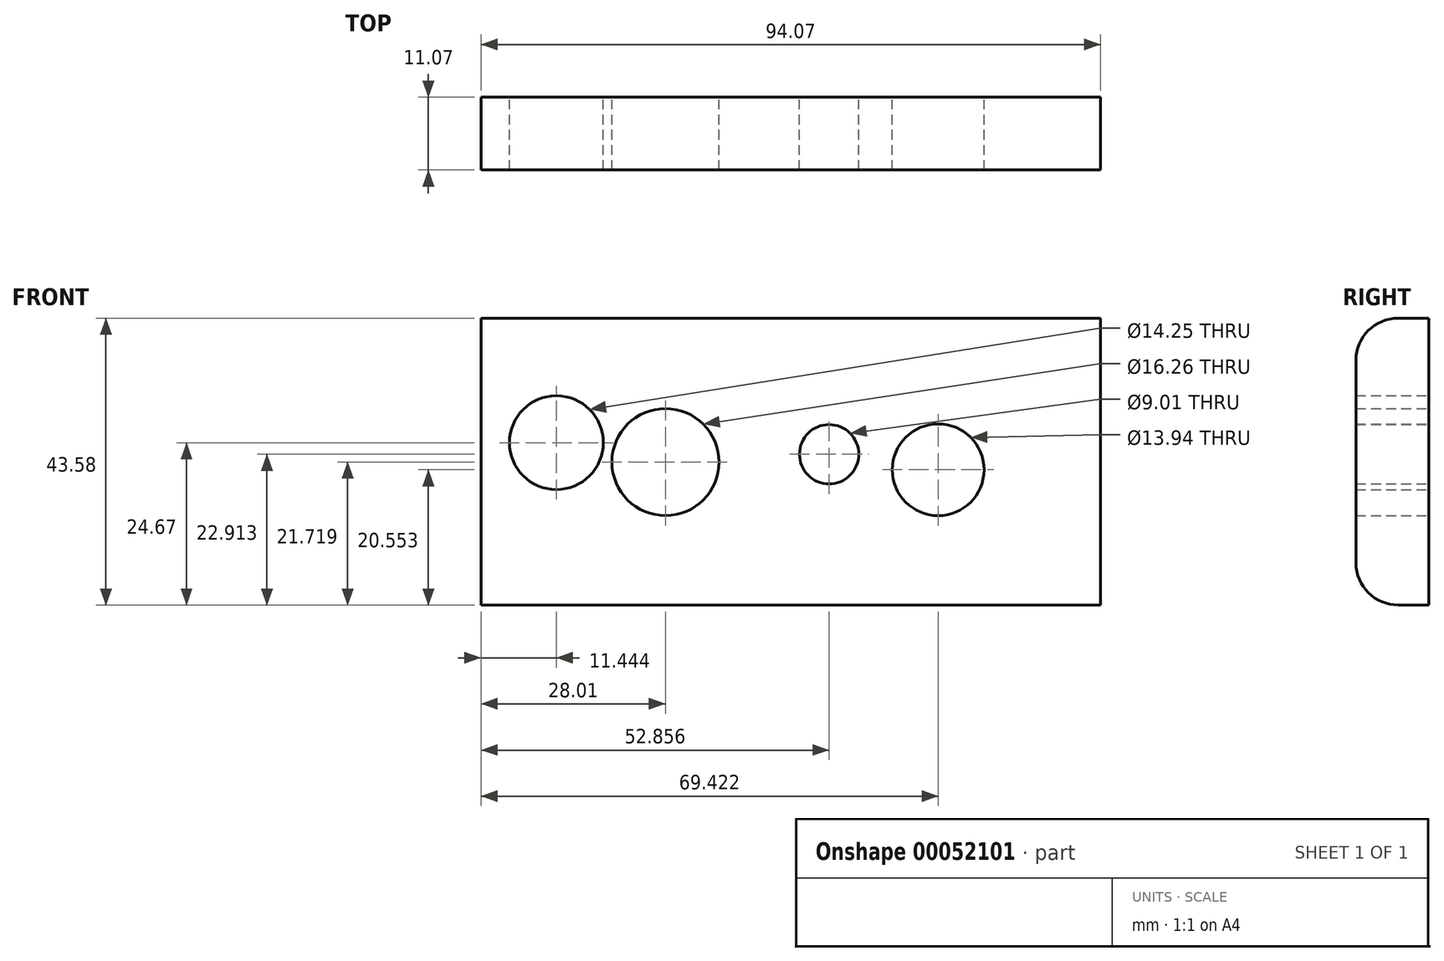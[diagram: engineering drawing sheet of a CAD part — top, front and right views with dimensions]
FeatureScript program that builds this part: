
annotation { "Feature Type Name" : "Feature", "Feature Type Description" : "" }
export const myFeature = defineFeature(function(context is Context, id is Id, definition is map)
    precondition{}
    {
        {
            var Q0;
            Q0=qCreatedBy(makeId("Front.planeOp"),FACE);
            var sketch = newSketch(context, id + "F0", { "sketchPlane" : qUnion([Q0])});
            skLineSegment(sketch, "E0.bottom", {"start": v(-38.08, 13.17) * mm, "end": v(55.99, 13.17) * mm});
            skLineSegment(sketch, "E0.top", {"start": v(-38.08, -30.4) * mm, "end": v(55.99, -30.4) * mm});
            skLineSegment(sketch, "E0.left", {"start": v(-38.08, 13.17) * mm, "end": v(-38.08, -30.4) * mm});
            skLineSegment(sketch, "E0.right", {"start": v(55.99, 13.17) * mm, "end": v(55.99, -30.4) * mm});
            skSolve(sketch);
        }
        {
            var Q0;
            Q0=makeQuery(id+"F0.imprint","IMPRINT",FACE,{"disambiguationData":[TD([[makeQuery(id+"F0.imprint","IMPRINT",EDGE,{"derivedFrom":sQuery(id+"F0.wireOp",EDGE,"E0.bottom")}),-1.0]])]});
            extrude(context, id + "F1", {"entities" : qUnion([Q0]), "depth" : 11.07 * mm});
        }
        {
            var Q0;
            Q0=qCreatedBy(makeId("Front.planeOp"),FACE);
            var sketch = newSketch(context, id + "F2", { "sketchPlane" : qUnion([Q0])});
            skCircle(sketch, "E1", {"center": v(-26.64, -5.74) * mm, "radius": 7.12 * mm});
            skCircle(sketch, "E2", {"center": v(-10.07, -8.7) * mm, "radius": 8.13 * mm});
            skCircle(sketch, "E3", {"center": v(14.78, -7.5) * mm, "radius": 4.5 * mm});
            skCircle(sketch, "E4", {"center": v(31.34, -9.86) * mm, "radius": 6.97 * mm});
            skSolve(sketch);
        }
        {
            var Q0;
            Q0=makeQuery(id+"F2.imprint","IMPRINT",FACE,{"disambiguationData":[TD([[makeQuery(id+"F2.imprint","IMPRINT",EDGE,{"derivedFrom":sQuery(id+"F2.wireOp",EDGE,"E4")}),1.0]])]});
            var Q1;
            Q1=makeQuery(id+"F2.imprint","IMPRINT",FACE,{"disambiguationData":[TD([[makeQuery(id+"F2.imprint","IMPRINT",EDGE,{"derivedFrom":sQuery(id+"F2.wireOp",EDGE,"E3")}),1.0]])]});
            var Q2;
            Q2=makeQuery(id+"F2.imprint","IMPRINT",FACE,{"disambiguationData":[TD([[makeQuery(id+"F2.imprint","IMPRINT",EDGE,{"derivedFrom":sQuery(id+"F2.wireOp",EDGE,"E2")}),1.0]])]});
            var Q3;
            Q3=makeQuery(id+"F2.imprint","IMPRINT",FACE,{"disambiguationData":[TD([[makeQuery(id+"F2.imprint","IMPRINT",EDGE,{"derivedFrom":sQuery(id+"F2.wireOp",EDGE,"E1")}),1.0]])]});
            var Q4;
            Q4=sQuery(id+"F2.wireOp",EDGE,"E1");
            var Q5;
            Q5=sQuery(id+"F2.wireOp",EDGE,"E2");
            var Q6;
            Q6=sQuery(id+"F2.wireOp",EDGE,"E3");
            var Q7;
            Q7=sQuery(id+"F2.wireOp",EDGE,"E4");
            extrude(context, id + "F3", {"entities" : qUnion([Q0, Q1, Q2, Q3]), "operationType" : NewBodyOperationType.REMOVE, "surfaceEntities" : qUnion([Q4, Q5, Q6, Q7]), "endBound" : BoundingType.UP_TO_NEXT, "depth" : 25.4 * mm});
        }
        {
            var Q0;
            Q0=makeQuery(id+"F1.opExtrude","CAP_EDGE",EDGE,{"disambiguationData":[OSD([sQuery(id+"F0.wireOp",EDGE,"E0.bottom")])],"isStart":false});
            var Q1;
            Q1=makeQuery(id+"F1.opExtrude","CAP_EDGE",EDGE,{"disambiguationData":[OSD([sQuery(id+"F0.wireOp",EDGE,"E0.top")])],"isStart":false});
            fillet(context, id + "F4", {"entities" : qUnion([Q0, Q1]), "radius" : 6.43 * mm, "tangentPropagation" : true, "allowEdgeOverflow" : false});
        }
    });
